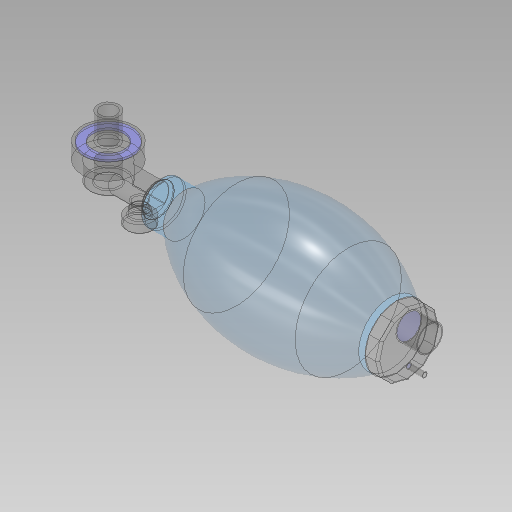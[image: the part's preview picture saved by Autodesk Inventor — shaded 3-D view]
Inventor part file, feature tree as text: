
AUTODESK INVENTOR PART (.ipt)
format: ipt  version: 2019 (Build 230136000, 136)  size: 298,496 bytes
history: native  units: mm
features: other x1, fillet x1
ambient origin geometry x8: Origin, YZ Plane, XZ Plane, XY Plane, X Axis, Y Axis, Z Axis, Center Point
bodies: Body1 (feature_tree)
feature tree (2):
  other  "Sólido1"
  fillet  "Fillet9"  [1 undecoded]
note: 1 required parameter value undecoded (feature->parameter linkage not recoverable at this tier; creation-order binding heuristic only, values carry confidence <= 0.55)
